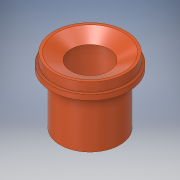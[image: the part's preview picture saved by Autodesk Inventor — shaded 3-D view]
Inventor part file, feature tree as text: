
AUTODESK INVENTOR PART (.ipt)
format: ipt  version: 2017 (Build 210142000, 142)  size: 168,448 bytes
history: native  units: in
note: dims shown in document units (in); Inventor stores cm internally (conversion verified against a paired STEP export)
features: revolve x1, sketch x1
ambient origin geometry x8: Origin, YZ Plane, XZ Plane, XY Plane, X Axis, Y Axis, Z Axis, Center Point
bodies: Body1 (feature_tree)
feature tree (2):
  revolve  "Revolution2"  [1 undecoded]
  sketch  "Sketch1"  dims[d0=1.13in d1=3.75in d2=0.25in d3=0.1718in d5=1.0in d6=1.0in d7=90.0deg d8=0.5in d9=15.0deg d11=0.25in d12=1.25in d13=0.25in d15=0.25in d16=0.5in d17=0.5in d18=0.5in d19=2.5in d20=0.5in d22=0.375in d23=0.25in d25=0.234in d26=15.0deg d28=90.0deg]
note: 1 required parameter value undecoded (feature->parameter linkage not recoverable at this tier; creation-order binding heuristic only, values carry confidence <= 0.55)
